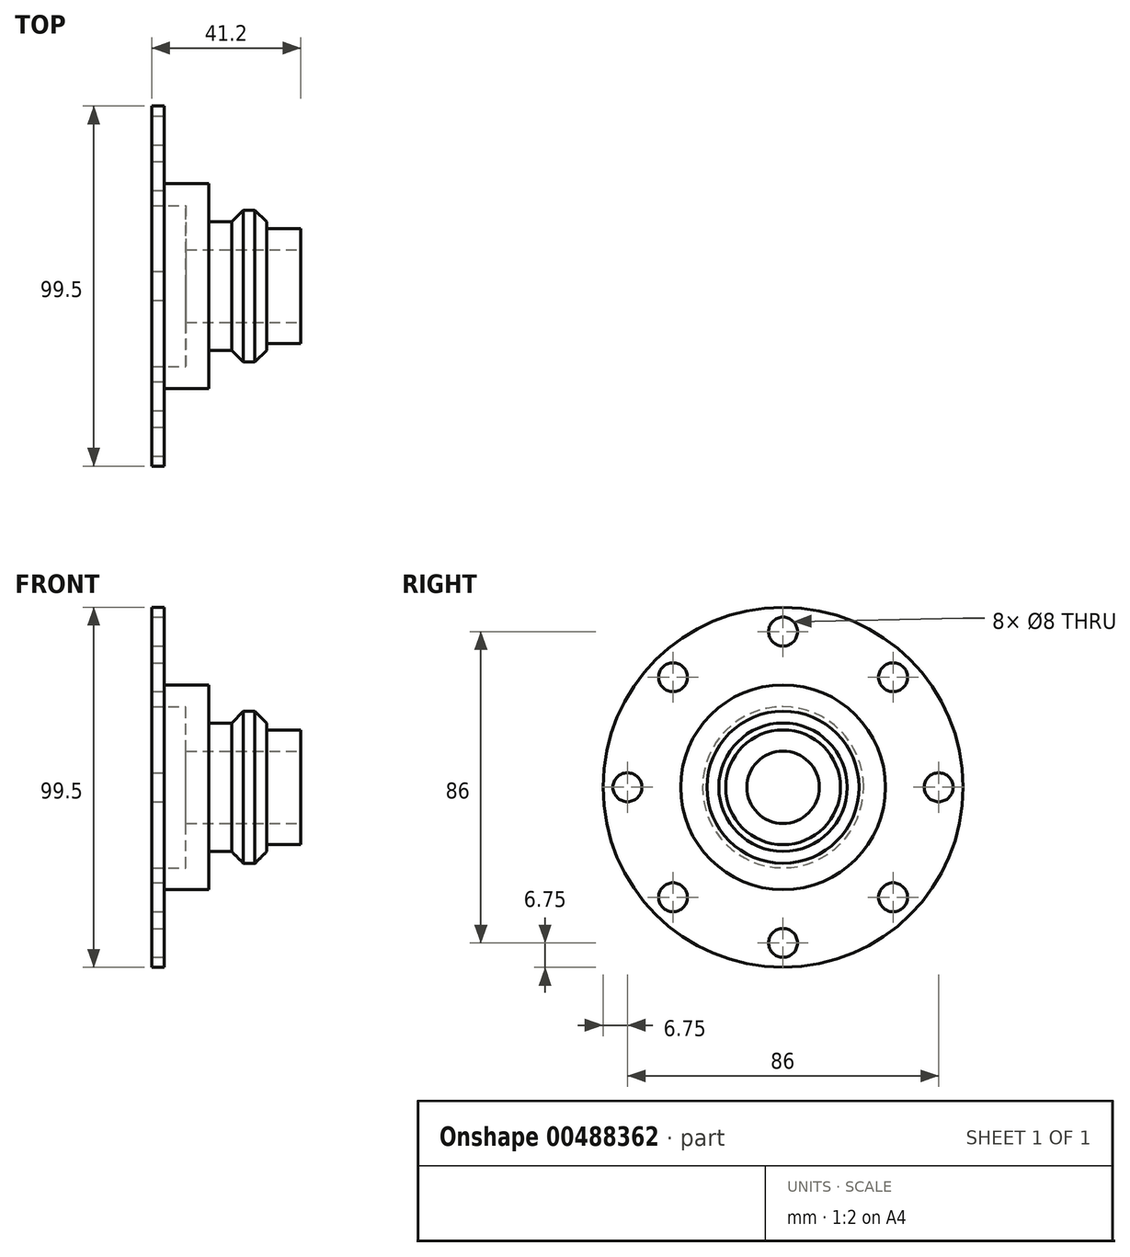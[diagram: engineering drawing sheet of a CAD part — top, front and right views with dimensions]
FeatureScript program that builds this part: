
annotation { "Feature Type Name" : "Feature", "Feature Type Description" : "" }
export const myFeature = defineFeature(function(context is Context, id is Id, definition is map)
    precondition{}
    {
        {
            var Q0;
            Q0=qCreatedBy(makeId("Front.planeOp"),FACE);
            var sketch = newSketch(context, id + "F0", { "sketchPlane" : qUnion([Q0])});
            skLineSegment(sketch, "E0.bottom", {"start": v(0, 0) * mm, "end": v(-41.2, 0) * mm, "construction": true});
            skLineSegment(sketch, "E0.top", {"start": v(-37.7, 49.75) * mm, "end": v(-41.2, 49.75) * mm});
            skLineSegment(sketch, "E0.left", {"start": v(0, 0) * mm, "end": v(0, 15.85) * mm});
            skLineSegment(sketch, "E0.right", {"start": v(-41.2, 0) * mm, "end": v(-41.2, 49.75) * mm});
            skLineSegment(sketch, "E1", {"start": v(-19.1, 17.75) * mm, "end": v(-25.4, 17.75) * mm});
            skLineSegment(sketch, "E2", {"start": v(-25.4, 17.75) * mm, "end": v(-25.4, 28.3) * mm});
            skLineSegment(sketch, "E3", {"start": v(-25.4, 28.3) * mm, "end": v(-37.7, 28.3) * mm});
            skLineSegment(sketch, "E4", {"start": v(-37.7, 28.3) * mm, "end": v(-37.7, 49.75) * mm});
            skLineSegment(sketch, "E5", {"start": v(-9.4, 15.85) * mm, "end": v(0, 15.85) * mm});
            skLineSegment(sketch, "E6", {"start": v(-9.4, 15.85) * mm, "end": v(-9.4, 17.75) * mm});
            skLineSegment(sketch, "E7", {"start": v(-9.4, 17.75) * mm, "end": v(-12.65, 21) * mm});
            skLineSegment(sketch, "E8", {"start": v(-12.65, 21) * mm, "end": v(-15.85, 21) * mm});
            skLineSegment(sketch, "E9", {"start": v(-15.85, 21) * mm, "end": v(-19.1, 17.75) * mm});
            skLineSegment(sketch, "E10", {"start": v(-41.2, 22.25) * mm, "end": v(-31.7, 22.25) * mm});
            skLineSegment(sketch, "E11", {"start": v(-31.7, 22.25) * mm, "end": v(-31.7, 10) * mm});
            skLineSegment(sketch, "E12", {"start": v(-31.7, 10) * mm, "end": v(0, 10) * mm});
            skSolve(sketch);
        }
        {
            var Q0;
            Q0 = qSketchRegion(id + "F0", true);
            var Q1;
            Q1=sQuery(id+"F0.wireOp",EDGE,"E0.bottom");
            revolve(context, id + "F1", {"entities" : qUnion([Q0]), "axis" : qUnion([Q1]), "revolveType" : RevolveType.FULL});
        }
        {
            var Q0;
            Q0=makeQuery(id+"F1.opRevolve","SWEPT_FACE",FACE,{"disambiguationData":[OSD([sQuery(id+"F0.wireOp",EDGE,"E4")])]});
            var sketch = newSketch(context, id + "F2", { "sketchPlane" : qUnion([Q0])});
            skCircle(sketch, "E13", {"center": v(0, 0) * mm, "radius": 43 * mm, "construction": true});
            skCircle(sketch, "E14", {"center": v(0, 43) * mm, "radius": 4 * mm});
            skCircle(sketch, "E15.1.0", {"center": v(-30.4, 30.4) * mm, "radius": 4 * mm});
            skCircle(sketch, "E15.2.0", {"center": v(-43, 0) * mm, "radius": 4 * mm});
            skCircle(sketch, "E16.1.3.0", {"center": v(-30.4, -30.4) * mm, "radius": 4 * mm});
            skCircle(sketch, "E16.1.4.0", {"center": v(0, -43) * mm, "radius": 4 * mm});
            skCircle(sketch, "E16.1.5.0", {"center": v(30.4, -30.4) * mm, "radius": 4 * mm});
            skCircle(sketch, "E16.1.6.0", {"center": v(43, 0) * mm, "radius": 4 * mm});
            skCircle(sketch, "E16.1.7.0", {"center": v(30.4, 30.4) * mm, "radius": 4 * mm});
            skLineSegment(sketch, "E17", {"start": v(0, 43) * mm, "end": v(0, 0) * mm, "construction": true});
            skLineSegment(sketch, "E18", {"start": v(-30.4, 30.4) * mm, "end": v(0, 0) * mm, "construction": true});
            skLineSegment(sketch, "E19", {"start": v(-43, 0) * mm, "end": v(0, 0) * mm, "construction": true});
            skLineSegment(sketch, "E20", {"start": v(-30.4, -30.4) * mm, "end": v(0, 0) * mm, "construction": true});
            skSolve(sketch);
        }
        {
            var Q0;
            Q0 = qSketchRegion(id + "F2", true);
            extrude(context, id + "F3", {"entities" : qUnion([Q0]), "operationType" : NewBodyOperationType.REMOVE, "endBound" : BoundingType.THROUGH_ALL, "oppositeDirection" : true, "depth" : 25 * mm});
        }
    });
